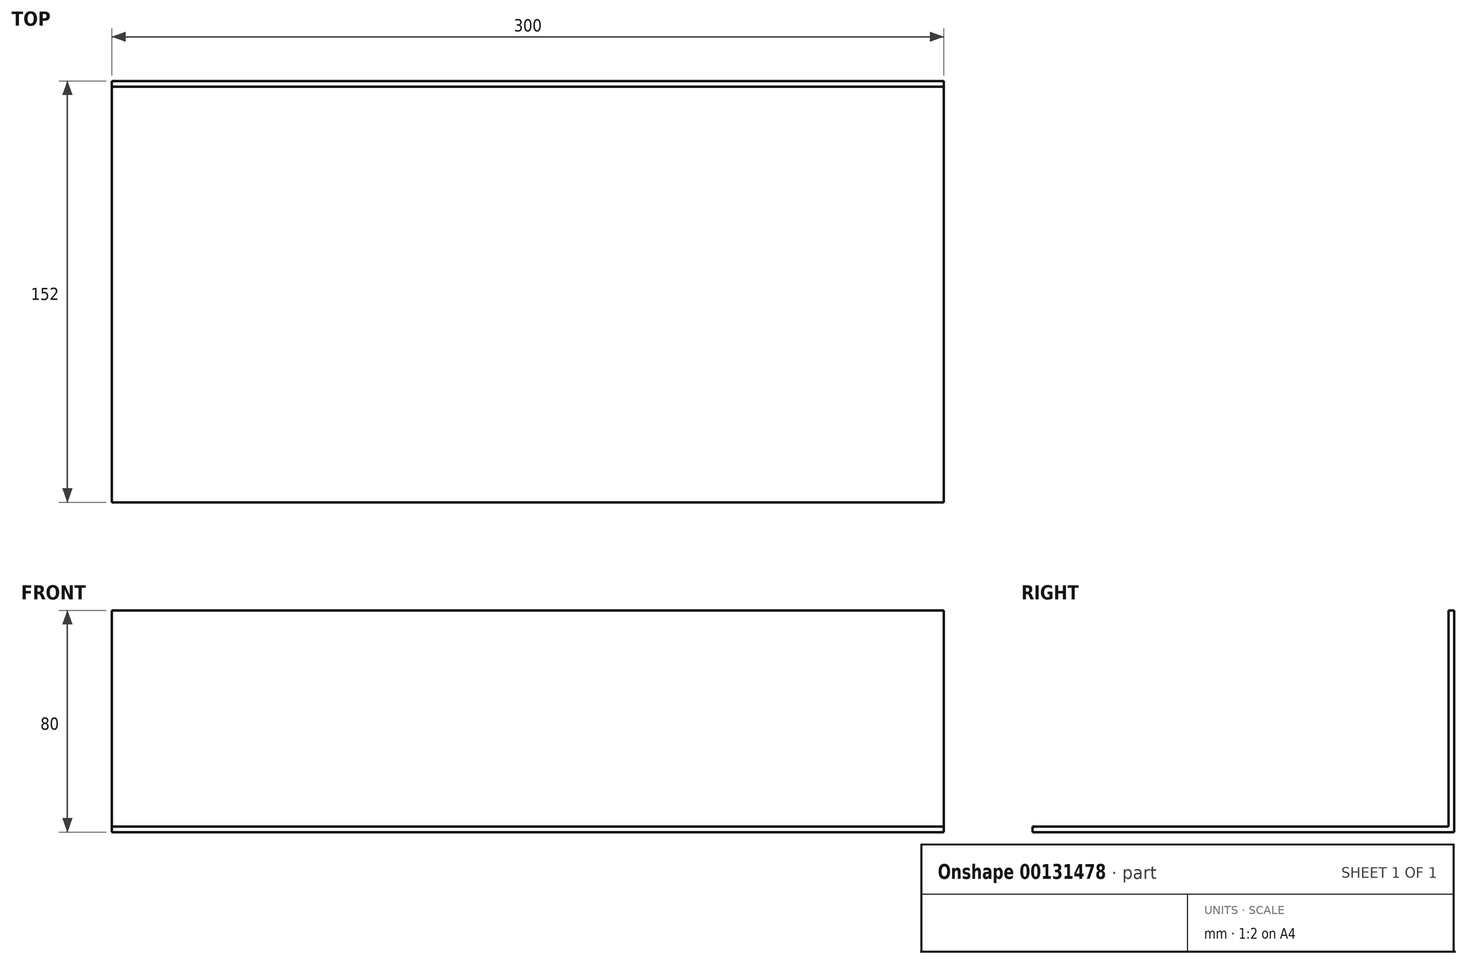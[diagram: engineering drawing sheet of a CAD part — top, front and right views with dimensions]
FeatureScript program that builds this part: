
annotation { "Feature Type Name" : "Feature", "Feature Type Description" : "" }
export const myFeature = defineFeature(function(context is Context, id is Id, definition is map)
    precondition{}
    {
        {
            var Q0;
            Q0=qCreatedBy(makeId("Front.planeOp"),FACE);
            var sketch = newSketch(context, id + "F0", { "sketchPlane" : qUnion([Q0])});
            skLineSegment(sketch, "E0.bottom", {"start": v(0, 0) * mm, "end": v(300, 0) * mm});
            skLineSegment(sketch, "E0.top", {"start": v(0, 80) * mm, "end": v(300, 80) * mm});
            skLineSegment(sketch, "E0.left", {"start": v(0, 0) * mm, "end": v(0, 80) * mm});
            skLineSegment(sketch, "E0.right", {"start": v(300, 0) * mm, "end": v(300, 80) * mm});
            skSolve(sketch);
        }
        {
            var Q0;
            Q0=makeQuery(id+"F0.imprint","IMPRINT",FACE,{"disambiguationData":[TD([[makeQuery(id+"F0.imprint","IMPRINT",EDGE,{"derivedFrom":sQuery(id+"F0.wireOp",EDGE,"E0.bottom")}),1.0]])]});
            extrude(context, id + "F1", {"entities" : qUnion([Q0]), "depth" : 2 * mm});
        }
        {
            var Q0;
            Q0=makeQuery(id+"F1.opExtrude","CAP_FACE",FACE,{"disambiguationData":[OSD([sQuery(id+"F0.wireOp",EDGE,"E0.bottom"),sQuery(id+"F0.wireOp",EDGE,"E0.top"),sQuery(id+"F0.wireOp",EDGE,"E0.left"),sQuery(id+"F0.wireOp",EDGE,"E0.right")])],"isStart":false});
            var sketch = newSketch(context, id + "F2", { "sketchPlane" : qUnion([Q0])});
            skLineSegment(sketch, "E1.bottom", {"start": v(0, 0) * mm, "end": v(300, 0) * mm});
            skLineSegment(sketch, "E1.top", {"start": v(0, 2) * mm, "end": v(300, 2) * mm});
            skLineSegment(sketch, "E1.left", {"start": v(0, 0) * mm, "end": v(0, 2) * mm});
            skLineSegment(sketch, "E1.right", {"start": v(300, 0) * mm, "end": v(300, 2) * mm});
            skSolve(sketch);
        }
        {
            var Q0;
            Q0 = qSketchRegion(id + "F2", true);
            extrude(context, id + "F3", {"entities" : qUnion([Q0]), "operationType" : NewBodyOperationType.ADD, "depth" : 150 * mm});
        }
    });
